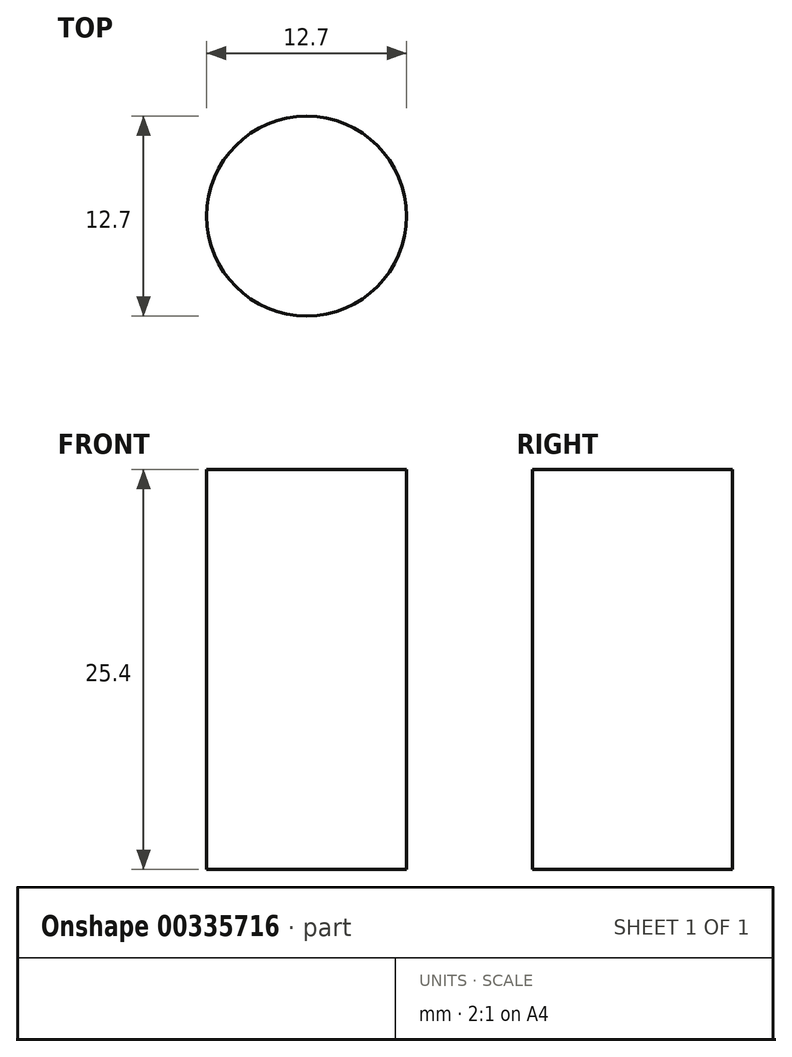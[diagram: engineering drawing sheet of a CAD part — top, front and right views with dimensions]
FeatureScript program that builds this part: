
annotation { "Feature Type Name" : "Feature", "Feature Type Description" : "" }
export const myFeature = defineFeature(function(context is Context, id is Id, definition is map)
    precondition{}
    {
        {
            var Q0;
            Q0=qCreatedBy(makeId("Top.planeOp"),FACE);
            var sketch = newSketch(context, id + "F0", { "sketchPlane" : qUnion([Q0])});
            skCircle(sketch, "E0", {"center": v(-35.68, 25.96) * mm, "radius": 5.82 * mm});
            skLineSegment(sketch, "E1.bottom", {"start": v(8.81, 17.97) * mm, "end": v(27.82, 17.97) * mm});
            skLineSegment(sketch, "E1.top", {"start": v(8.81, 6.74) * mm, "end": v(27.82, 6.74) * mm});
            skLineSegment(sketch, "E1.left", {"start": v(8.81, 17.97) * mm, "end": v(8.81, 6.74) * mm});
            skLineSegment(sketch, "E1.right", {"start": v(27.82, 17.97) * mm, "end": v(27.82, 6.74) * mm});
            skLineSegment(sketch, "E2", {"start": v(-31.89, -10.43) * mm, "end": v(-14.18, -16.48) * mm});
            skLineSegment(sketch, "E3", {"start": v(-14.18, -16.48) * mm, "end": v(-14.18, -34.2) * mm});
            skLineSegment(sketch, "E4", {"start": v(-14.18, -34.2) * mm, "end": v(-34.48, -37.43) * mm});
            skLineSegment(sketch, "E5", {"start": v(-34.48, -37.43) * mm, "end": v(-31.89, -10.43) * mm});
            skLineSegment(sketch, "E6", {"start": v(-26.49, -18) * mm, "end": v(-29.51, -30.09) * mm});
            skLineSegment(sketch, "E7", {"start": v(-29.51, -30.09) * mm, "end": v(-23, -31.71) * mm});
            skLineSegment(sketch, "E8", {"start": v(-23, -31.71) * mm, "end": v(-26.49, -18) * mm});
            skCircle(sketch, "E9", {"center": v(-31.5, 13.4) * mm, "radius": 6.35 * mm});
            skSolve(sketch);
        }
        {
            var Q0;
            Q0=makeQuery(id+"F0.imprint","IMPRINT",FACE,{"disambiguationData":[TD([[makeQuery(id+"F0.imprint","IMPRINT",EDGE,{"derivedFrom":sQuery(id+"F0.wireOp",EDGE,"E9")}),1.0]])]});
            extrude(context, id + "F1", {"entities" : qUnion([Q0]), "depth" : 25.4 * mm});
        }
    });
